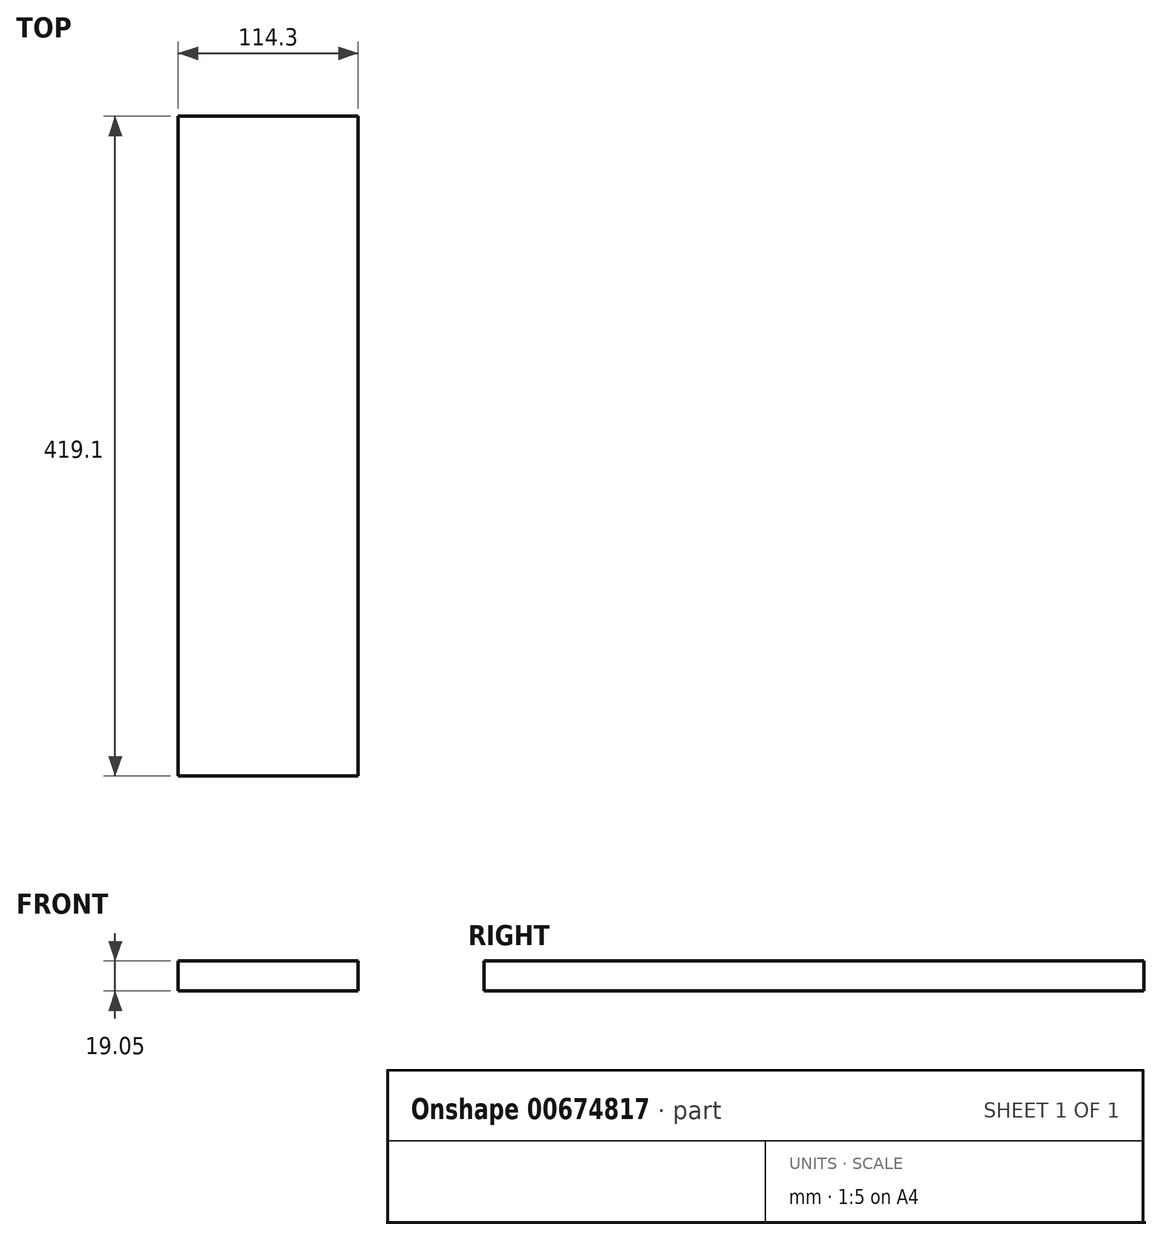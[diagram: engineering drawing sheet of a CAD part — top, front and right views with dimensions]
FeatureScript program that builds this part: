
annotation { "Feature Type Name" : "Feature", "Feature Type Description" : "" }
export const myFeature = defineFeature(function(context is Context, id is Id, definition is map)
    precondition{}
    {
        {
            var Q0;
            Q0=qCreatedBy(makeId("Top.planeOp"),FACE);
            var sketch = newSketch(context, id + "F0", { "sketchPlane" : qUnion([Q0])});
            skLineSegment(sketch, "E0.bottom", {"start": v(-57.15, -209.55) * mm, "end": v(57.15, -209.55) * mm});
            skLineSegment(sketch, "E0.top", {"start": v(-57.15, 209.55) * mm, "end": v(57.15, 209.55) * mm});
            skLineSegment(sketch, "E0.left", {"start": v(-57.15, -209.55) * mm, "end": v(-57.15, 209.55) * mm});
            skLineSegment(sketch, "E0.right", {"start": v(57.15, -209.55) * mm, "end": v(57.15, 209.55) * mm});
            skPoint(sketch, "E0.middle", {"position": v(0, 0) * mm});
            skSolve(sketch);
        }
        {
            var Q0;
            Q0=makeQuery(id+"F0.imprint","IMPRINT",FACE,{"disambiguationData":[TD([[makeQuery(id+"F0.imprint","IMPRINT",EDGE,{"derivedFrom":sQuery(id+"F0.wireOp",EDGE,"E0.bottom")}),1.0]])]});
            extrude(context, id + "F1", {"entities" : qUnion([Q0]), "depth" : 19.05 * mm, "offsetDistance" : 25.4 * mm});
        }
    });
